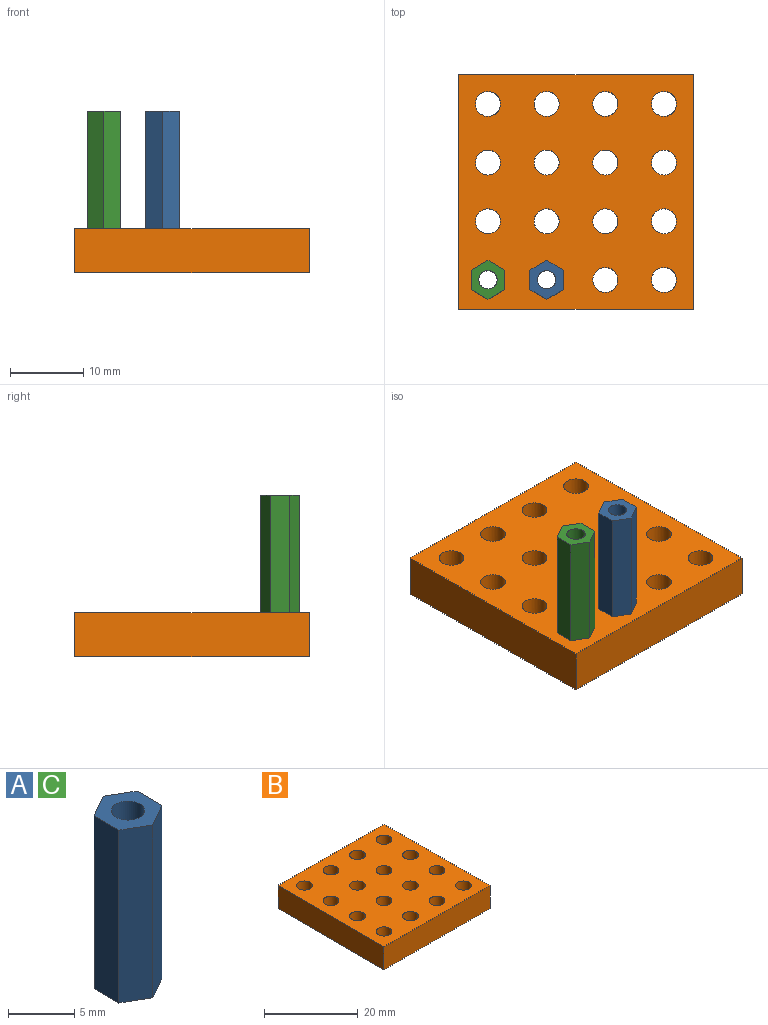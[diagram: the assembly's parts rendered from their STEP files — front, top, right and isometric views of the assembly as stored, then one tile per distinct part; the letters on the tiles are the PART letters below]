
ASSEMBLY  parts=3 mates=2
PART A: 9 faces, bbox 4.6x5.3x16 mm
  f0: plane 16x2.3mm, normal (0.5,-0.87,0), area 42.5mm2, adj f1,f5,f6,f7
  f1: plane 16x2.66mm, normal (1,0,0), area 42.5mm2, adj f0,f2,f6,f7
  f2: plane 16x2.3mm, normal (0.5,0.87,0), area 42.5mm2, adj f1,f3,f6,f7
  f3: plane 16x2.3mm, normal (-0.5,0.87,0), area 42.5mm2, adj f2,f4,f6,f7
  f4: plane 16x2.66mm, normal (-1,0,0), area 42.5mm2, adj f3,f5,f6,f7
  f5: plane 16x2.3mm, normal (-0.5,-0.87,0), area 42.5mm2, adj f0,f4,f6,f7
  f6: plane 5.31x4.6mm, normal (0,0,1), area 13.4mm2, adj f0,f1,f2,f3,f4,f5,f8
  f7: plane 5.31x4.6mm, normal (0,0,-1), area 13.4mm2, adj f0,f1,f2,f3,f4,f5,f8
  f8: cylinder r=1.25mm len=16mm, axis (0,0,-1), area 125.7mm2, adj f6,f7
PART B: 22 faces, bbox 32x32x6 mm
  f0: plane 32x6mm, normal (0,-1,0), area 192mm2, adj f1,f2,f3,f7
  f1: plane 32x6mm, normal (-1,0,0), area 192mm2, adj f0,f2,f3,f17
  f2: plane 32x32mm, normal (0,0,1), area 878.7mm2, adj f0,f1,f4,f5,f6,f7,f8,f9
  f3: plane 32x32mm, normal (0,0,-1), area 878.7mm2, adj f0,f1,f4,f5,f6,f7,f8,f9
  f4: cylinder r=1.7mm len=6mm, axis (0,0,-1), area 64.1mm2, adj f2,f3
  f5: cylinder r=1.7mm len=6mm, axis (0,0,-1), area 64.1mm2, adj f2,f3
  f6: cylinder r=1.7mm len=6mm, axis (0,0,-1), area 64.1mm2, adj f2,f3
  f7: plane 32x6mm, normal (1,0,0), area 192mm2, adj f0,f2,f3,f17
  f8: cylinder r=1.7mm len=6mm, axis (0,0,-1), area 64.1mm2, adj f2,f3
  f9: cylinder r=1.7mm len=6mm, axis (0,0,-1), area 64.1mm2, adj f2,f3
  f10: cylinder r=1.7mm len=6mm, axis (0,0,-1), area 64.1mm2, adj f2,f3
  f11: cylinder r=1.7mm len=6mm, axis (0,0,-1), area 64.1mm2, adj f2,f3
  f12: cylinder r=1.7mm len=6mm, axis (0,0,-1), area 64.1mm2, adj f2,f3
  f13: cylinder r=1.7mm len=6mm, axis (0,0,-1), area 64.1mm2, adj f2,f3
  f14: cylinder r=1.7mm len=6mm, axis (0,0,-1), area 64.1mm2, adj f2,f3
  f15: cylinder r=1.7mm len=6mm, axis (0,0,-1), area 64.1mm2, adj f2,f3
  f16: cylinder r=1.7mm len=6mm, axis (0,0,-1), area 64.1mm2, adj f2,f3
  f17: plane 32x6mm, normal (0,1,0), area 192mm2, adj f1,f2,f3,f7
  f18: cylinder r=1.7mm len=6mm, axis (0,0,-1), area 64.1mm2, adj f2,f3
  f19: cylinder r=1.7mm len=6mm, axis (0,0,-1), area 64.1mm2, adj f2,f3
  f20: cylinder r=1.7mm len=6mm, axis (0,0,-1), area 64.1mm2, adj f2,f3
  f21: cylinder r=1.7mm len=6mm, axis (0,0,-1), area 64.1mm2, adj f2,f3
PART C: same geometry as A
PLACE A t=(-3.2,-14.6,-1.58)mm
PLACE B t=(-11.2,-14.6,-7.58)mm
PLACE C t=(-11.2,-14.6,-1.58)mm
MATE fastened B.f5 <-> B.f2  axis (0,0,-1) through (-3.2,-14.6,-1.58)mm
MATE fastened C.f8 <-> B.f4  axis (0,0,1) through (-11.2,-14.6,-1.58)mm
